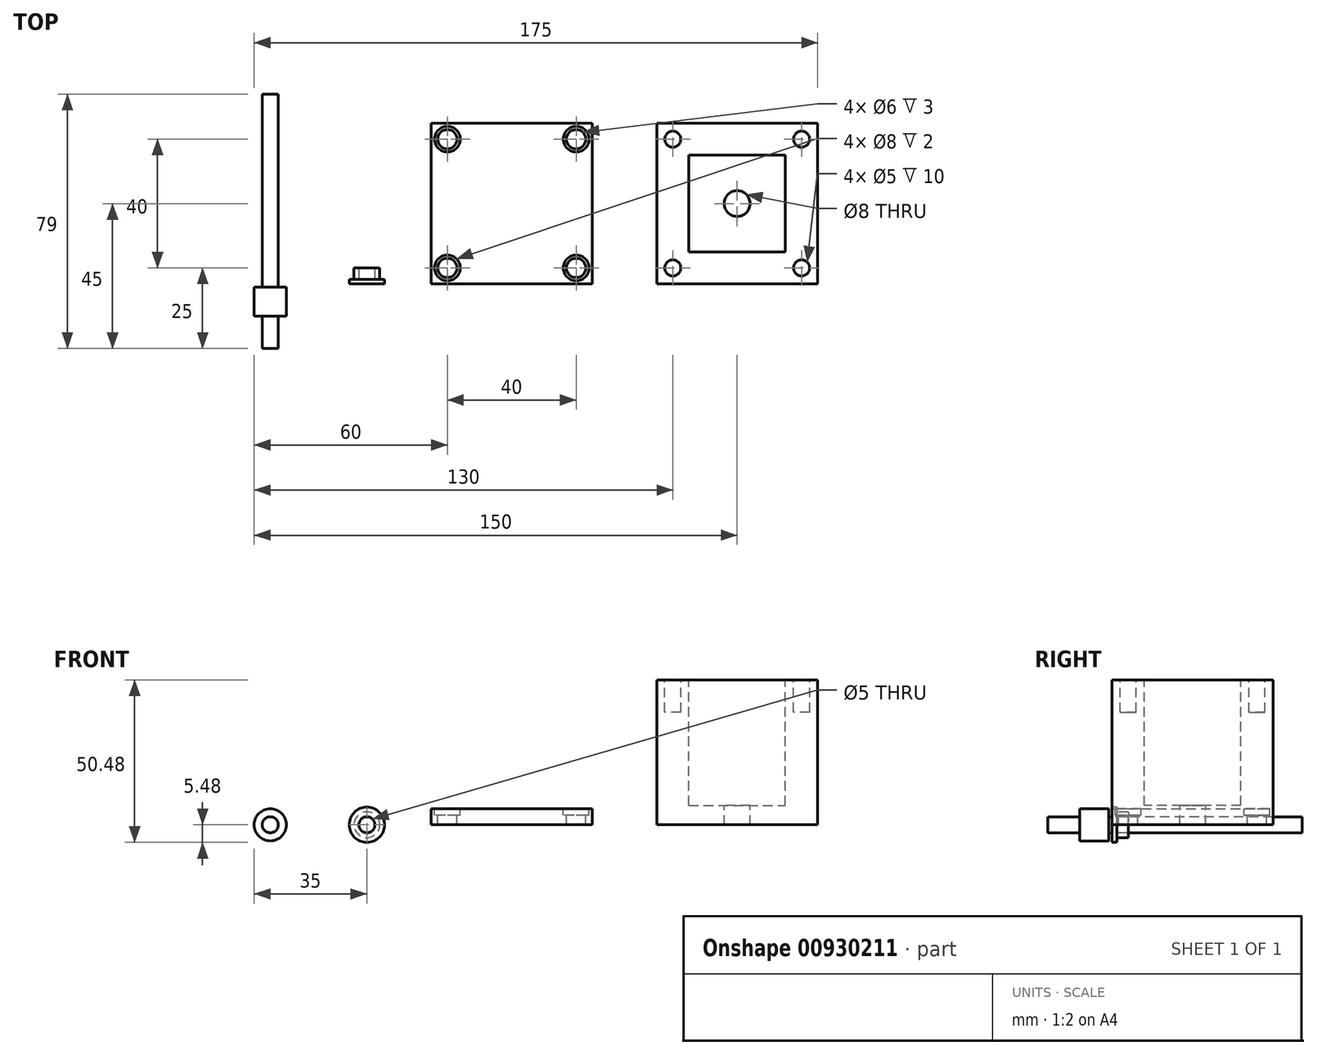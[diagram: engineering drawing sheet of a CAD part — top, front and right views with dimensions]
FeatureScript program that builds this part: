
annotation { "Feature Type Name" : "Feature", "Feature Type Description" : "" }
export const myFeature = defineFeature(function(context is Context, id is Id, definition is map)
    precondition{}
    {
        {
            var Q0;
            Q0=qCreatedBy(makeId("Top.planeOp"),FACE);
            var sketch = newSketch(context, id + "F0", { "sketchPlane" : qUnion([Q0])});
            skLineSegment(sketch, "E0.bottom", {"start": v(0, 0) * mm, "end": v(50, 0) * mm});
            skLineSegment(sketch, "E0.top", {"start": v(0, 50) * mm, "end": v(50, 50) * mm});
            skLineSegment(sketch, "E0.left", {"start": v(0, 0) * mm, "end": v(0, 50) * mm});
            skLineSegment(sketch, "E0.right", {"start": v(50, 0) * mm, "end": v(50, 50) * mm});
            skSolve(sketch);
        }
        {
            var Q0;
            Q0 = qSketchRegion(id + "F0", true);
            extrude(context, id + "F1", {"entities" : qUnion([Q0]), "depth" : 45 * mm, "offsetDistance" : 25 * mm});
        }
        {
            var Q0;
            Q0=makeQuery(id+"F1.opExtrude","CAP_FACE",FACE,{"disambiguationData":[OSD([sQuery(id+"F0.wireOp",EDGE,"E0.bottom"),sQuery(id+"F0.wireOp",EDGE,"E0.top"),sQuery(id+"F0.wireOp",EDGE,"E0.left"),sQuery(id+"F0.wireOp",EDGE,"E0.right")])],"isStart":false});
            var sketch = newSketch(context, id + "F2", { "sketchPlane" : qUnion([Q0])});
            skLineSegment(sketch, "E1", {"start": v(0, 0) * mm, "end": v(50, 50) * mm, "construction": true});
            skLineSegment(sketch, "E2", {"start": v(0, 50) * mm, "end": v(50, 0) * mm, "construction": true});
            skLineSegment(sketch, "E3.bottom", {"start": v(10, 40) * mm, "end": v(40, 40) * mm});
            skLineSegment(sketch, "E3.top", {"start": v(10, 10) * mm, "end": v(40, 10) * mm});
            skLineSegment(sketch, "E3.left", {"start": v(10, 40) * mm, "end": v(10, 10) * mm});
            skLineSegment(sketch, "E3.right", {"start": v(40, 40) * mm, "end": v(40, 10) * mm});
            skSolve(sketch);
        }
        {
            var Q0;
            Q0=makeQuery(id+"F2.imprint","IMPRINT",FACE,{"disambiguationData":[TD([[makeQuery(id+"F2.imprint","IMPRINT",EDGE,{"derivedFrom":sQuery(id+"F2.wireOp",EDGE,"E3.bottom")}),-1.0]])]});
            extrude(context, id + "F3", {"entities" : qUnion([Q0]), "operationType" : NewBodyOperationType.REMOVE, "oppositeDirection" : true, "depth" : 39 * mm, "offsetDistance" : 25 * mm});
        }
        {
            var Q0;
            Q0=makeQuery(id+"F1.opExtrude","CAP_FACE",FACE,{"disambiguationData":[OSD([sQuery(id+"F0.wireOp",EDGE,"E0.bottom"),sQuery(id+"F0.wireOp",EDGE,"E0.top"),sQuery(id+"F0.wireOp",EDGE,"E0.left"),sQuery(id+"F0.wireOp",EDGE,"E0.right")])],"isStart":false});
            var sketch = newSketch(context, id + "F4", { "sketchPlane" : qUnion([Q0])});
            skCircle(sketch, "E4", {"center": v(5, 45) * mm, "radius": 2.5 * mm});
            skLineSegment(sketch, "E5", {"start": v(0, 50) * mm, "end": v(50, 0) * mm, "construction": true});
            skLineSegment(sketch, "E6", {"start": v(50, 50) * mm, "end": v(0, 0) * mm, "construction": true});
            skLineSegment(sketch, "E7", {"start": v(0, 45) * mm, "end": v(50, 45) * mm, "construction": true});
            skLineSegment(sketch, "E8", {"start": v(25, 50) * mm, "end": v(25, 45) * mm, "construction": true});
            skLineSegment(sketch, "E9", {"start": v(25, 45) * mm, "end": v(25, 40) * mm, "construction": true});
            skLineSegment(sketch, "E10", {"start": v(0, 25) * mm, "end": v(50, 25) * mm, "construction": true});
            skCircle(sketch, "E11.MirrorC", {"center": v(5, 5) * mm, "radius": 2.5 * mm});
            skCircle(sketch, "E12.MirrorC", {"center": v(45, 45) * mm, "radius": 2.5 * mm});
            skCircle(sketch, "E13.MirrorC", {"center": v(45, 5) * mm, "radius": 2.5 * mm});
            skSolve(sketch);
        }
        {
            var Q0;
            Q0 = qSketchRegion(id + "F4", true);
            extrude(context, id + "F5", {"entities" : qUnion([Q0]), "operationType" : NewBodyOperationType.REMOVE, "oppositeDirection" : true, "depth" : 10 * mm, "offsetDistance" : 25 * mm});
        }
        {
            var Q0;
            Q0=makeQuery(id+"F3.boolean.opBoolean","COPY",FACE,{"derivedFrom":makeQuery(id+"F3.opExtrude","CAP_FACE",FACE,{"disambiguationData":[OSD([sQuery(id+"F2.wireOp",EDGE,"E3.bottom"),sQuery(id+"F2.wireOp",EDGE,"E3.top"),sQuery(id+"F2.wireOp",EDGE,"E3.left"),sQuery(id+"F2.wireOp",EDGE,"E3.right")])],"isStart":false})});
            var sketch = newSketch(context, id + "F6", { "sketchPlane" : qUnion([Q0])});
            skCircle(sketch, "E14", {"center": v(25, 25) * mm, "radius": 4 * mm});
            skLineSegment(sketch, "E15", {"start": v(25, 40) * mm, "end": v(25, 10) * mm, "construction": true});
            skLineSegment(sketch, "E16", {"start": v(10, 25) * mm, "end": v(40, 25) * mm, "construction": true});
            skSolve(sketch);
        }
        {
            var Q0;
            Q0 = qSketchRegion(id + "F6", true);
            extrude(context, id + "F7", {"entities" : qUnion([Q0]), "operationType" : NewBodyOperationType.REMOVE, "oppositeDirection" : true, "depth" : 25 * mm, "offsetDistance" : 25 * mm});
        }
        {
            var Q0;
            Q0=qCreatedBy(makeId("Top.planeOp"),FACE);
            var sketch = newSketch(context, id + "F8", { "sketchPlane" : qUnion([Q0])});
            skLineSegment(sketch, "E17.bottom", {"start": v(-70, 0) * mm, "end": v(-20, 0) * mm});
            skLineSegment(sketch, "E17.top", {"start": v(-70, 50) * mm, "end": v(-20, 50) * mm});
            skLineSegment(sketch, "E17.left", {"start": v(-70, 0) * mm, "end": v(-70, 50) * mm});
            skLineSegment(sketch, "E17.right", {"start": v(-20, 0) * mm, "end": v(-20, 50) * mm});
            skSolve(sketch);
        }
        {
            var Q0;
            Q0 = qSketchRegion(id + "F8", true);
            extrude(context, id + "F9", {"entities" : qUnion([Q0]), "depth" : 5 * mm, "offsetDistance" : 25 * mm});
        }
        {
            var Q0;
            Q0=makeQuery(id+"F9.opExtrude","CAP_FACE",FACE,{"disambiguationData":[OSD([sQuery(id+"F8.wireOp",EDGE,"E17.bottom"),sQuery(id+"F8.wireOp",EDGE,"E17.top"),sQuery(id+"F8.wireOp",EDGE,"E17.left"),sQuery(id+"F8.wireOp",EDGE,"E17.right")])],"isStart":false});
            var sketch = newSketch(context, id + "F10", { "sketchPlane" : qUnion([Q0])});
            skLineSegment(sketch, "E18", {"start": v(-70, 50) * mm, "end": v(-20, 0) * mm, "construction": true});
            skLineSegment(sketch, "E19", {"start": v(-20, 50) * mm, "end": v(-70, 0) * mm, "construction": true});
            skLineSegment(sketch, "E20", {"start": v(-20, 45) * mm, "end": v(-70, 45) * mm, "construction": true});
            skCircle(sketch, "E21", {"center": v(-65, 45) * mm, "radius": 3 * mm});
            skLineSegment(sketch, "E22", {"start": v(-60, 40) * mm, "end": v(-60, 10) * mm, "construction": true});
            skLineSegment(sketch, "E23", {"start": v(-60, 10) * mm, "end": v(-30, 10) * mm, "construction": true});
            skLineSegment(sketch, "E24", {"start": v(-30, 10) * mm, "end": v(-30, 40) * mm, "construction": true});
            skLineSegment(sketch, "E25", {"start": v(-30, 40) * mm, "end": v(-60, 40) * mm, "construction": true});
            skLineSegment(sketch, "E26", {"start": v(-45, 50) * mm, "end": v(-45, 45) * mm, "construction": true});
            skLineSegment(sketch, "E27", {"start": v(-45, 45) * mm, "end": v(-45, 40) * mm, "construction": true});
            skCircle(sketch, "E28.MirrorC", {"center": v(-25, 45) * mm, "radius": 3 * mm});
            skLineSegment(sketch, "E29", {"start": v(-70, 25) * mm, "end": v(-20, 25) * mm, "construction": true});
            skCircle(sketch, "E30.MirrorC", {"center": v(-25, 5) * mm, "radius": 3 * mm});
            skCircle(sketch, "E31.MirrorC", {"center": v(-65, 5) * mm, "radius": 3 * mm});
            skSolve(sketch);
        }
        {
            var Q0;
            Q0 = qSketchRegion(id + "F10", true);
            extrude(context, id + "F11", {"entities" : qUnion([Q0]), "operationType" : NewBodyOperationType.REMOVE, "oppositeDirection" : true, "depth" : 25 * mm, "offsetDistance" : 25 * mm});
        }
        {
            var Q0;
            Q0=makeQuery(id+"F9.opExtrude","CAP_FACE",FACE,{"disambiguationData":[OSD([sQuery(id+"F8.wireOp",EDGE,"E17.bottom"),sQuery(id+"F8.wireOp",EDGE,"E17.top"),sQuery(id+"F8.wireOp",EDGE,"E17.left"),sQuery(id+"F8.wireOp",EDGE,"E17.right")])],"isStart":false});
            var sketch = newSketch(context, id + "F12", { "sketchPlane" : qUnion([Q0])});
            skCircle(sketch, "E32", {"center": v(-65, 45) * mm, "radius": 4 * mm});
            skLineSegment(sketch, "E33", {"start": v(-45, 50) * mm, "end": v(-45, 0) * mm, "construction": true});
            skLineSegment(sketch, "E34", {"start": v(-70, 25) * mm, "end": v(-20, 25) * mm, "construction": true});
            skCircle(sketch, "E35.MirrorC", {"center": v(-65, 5) * mm, "radius": 4 * mm});
            skCircle(sketch, "E36.MirrorC", {"center": v(-25, 5) * mm, "radius": 4 * mm});
            skCircle(sketch, "E37.MirrorC", {"center": v(-25, 45) * mm, "radius": 4 * mm});
            skSolve(sketch);
        }
        {
            var Q0;
            Q0 = qSketchRegion(id + "F12", true);
            extrude(context, id + "F13", {"entities" : qUnion([Q0]), "operationType" : NewBodyOperationType.REMOVE, "oppositeDirection" : true, "depth" : 2 * mm, "offsetDistance" : 25 * mm});
        }
        {
            var Q0;
            Q0=qCreatedBy(makeId("Top.planeOp"),FACE);
            var sketch = newSketch(context, id + "F14", { "sketchPlane" : qUnion([Q0])});
            skLineSegment(sketch, "E38", {"start": v(-90, -15) * mm, "end": v(-90, 25) * mm, "construction": true});
            skLineSegment(sketch, "E39", {"start": v(-87.5, 0) * mm, "end": v(-84.52, 0) * mm});
            skLineSegment(sketch, "E40", {"start": v(-84.52, 0) * mm, "end": v(-84.52, 1.5) * mm});
            skLineSegment(sketch, "E41", {"start": v(-84.52, 1.5) * mm, "end": v(-86, 1.5) * mm});
            skLineSegment(sketch, "E42", {"start": v(-86, 1.5) * mm, "end": v(-86, 5) * mm});
            skLineSegment(sketch, "E43", {"start": v(-86, 5) * mm, "end": v(-87.5, 5) * mm});
            skLineSegment(sketch, "E44", {"start": v(-87.5, 5) * mm, "end": v(-87.5, 0) * mm});
            skSolve(sketch);
        }
        {
            var Q0;
            Q0 = qSketchRegion(id + "F14", true);
            var Q1;
            Q1=sQuery(id+"F14.wireOp",EDGE,"E38");
            revolve(context, id + "F15", {"surfaceOperationType" : NewSurfaceOperationType.NEW, "entities" : qUnion([Q0]), "axis" : qUnion([Q1]), "revolveType" : RevolveType.FULL});
        }
        {
            var Q0;
            Q0=qCreatedBy(makeId("Top.planeOp"),FACE);
            var sketch = newSketch(context, id + "F16", { "sketchPlane" : qUnion([Q0])});
            skLineSegment(sketch, "E45", {"start": v(-120, -30) * mm, "end": v(-120, 79.43) * mm, "construction": true});
            skLineSegment(sketch, "E46", {"start": v(-120, -20) * mm, "end": v(-117.5, -20) * mm});
            skLineSegment(sketch, "E47", {"start": v(-117.5, -20) * mm, "end": v(-117.5, -10) * mm});
            skLineSegment(sketch, "E48", {"start": v(-117.5, -10) * mm, "end": v(-115, -10) * mm});
            skLineSegment(sketch, "E49", {"start": v(-115, -10) * mm, "end": v(-115, -1) * mm});
            skLineSegment(sketch, "E50", {"start": v(-115, -1) * mm, "end": v(-117.5, -1) * mm});
            skLineSegment(sketch, "E51", {"start": v(-117.5, -1) * mm, "end": v(-117.5, 59) * mm});
            skLineSegment(sketch, "E52", {"start": v(-117.5, 59) * mm, "end": v(-120, 59) * mm});
            skLineSegment(sketch, "E53", {"start": v(-120, 59) * mm, "end": v(-120, -20) * mm});
            skSolve(sketch);
        }
        {
            var Q0;
            Q0 = qSketchRegion(id + "F16", true);
            var Q1;
            Q1=sQuery(id+"F16.wireOp",EDGE,"E45");
            revolve(context, id + "F17", {"surfaceOperationType" : NewSurfaceOperationType.NEW, "entities" : qUnion([Q0]), "axis" : qUnion([Q1]), "revolveType" : RevolveType.FULL});
        }
    });
